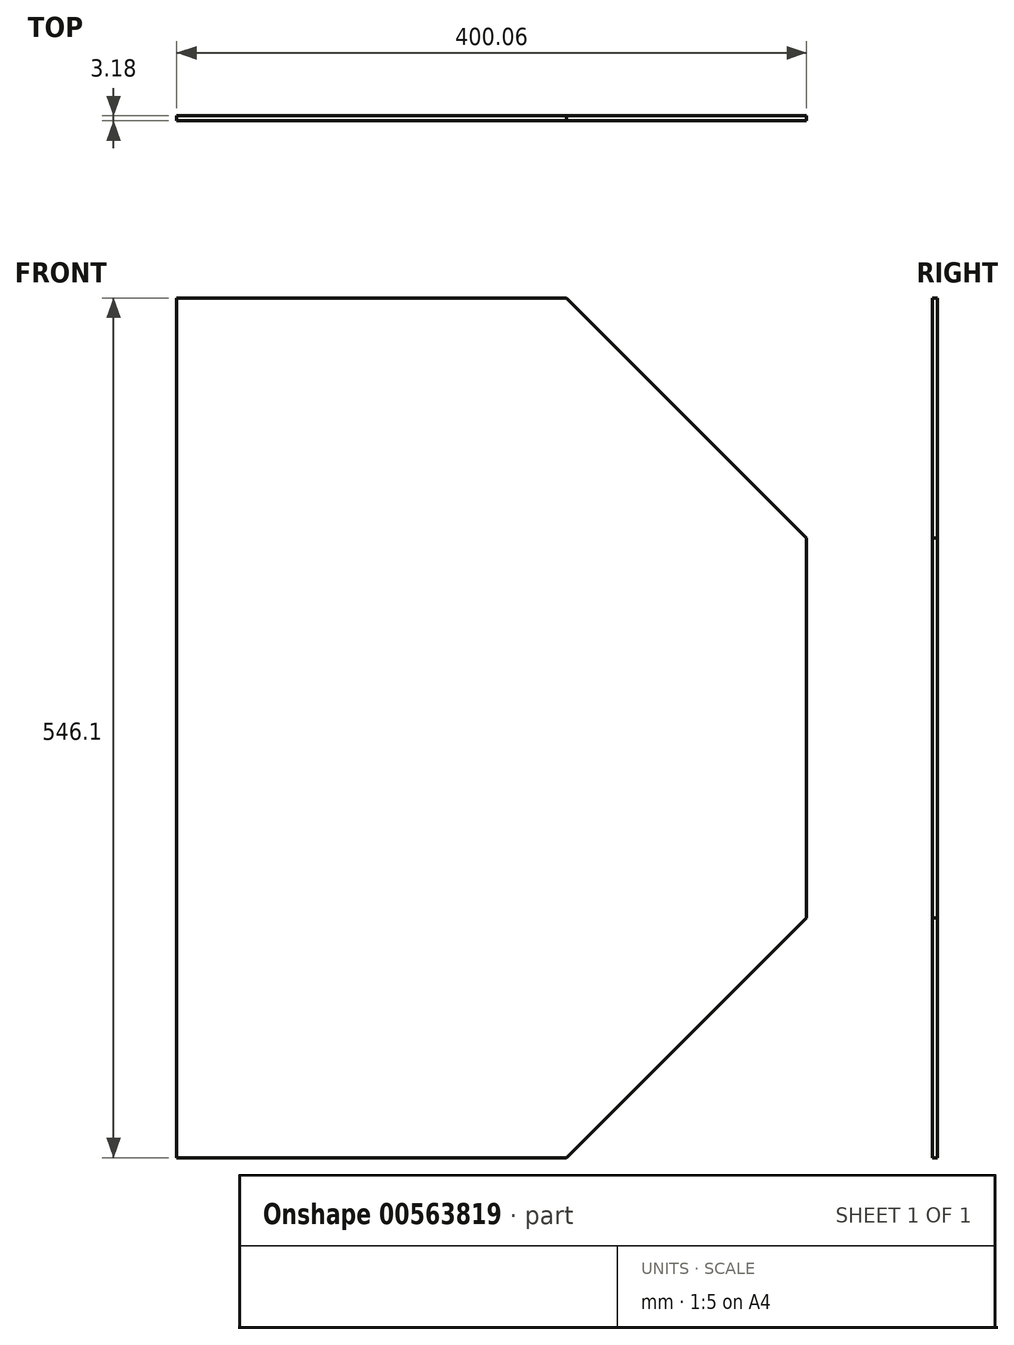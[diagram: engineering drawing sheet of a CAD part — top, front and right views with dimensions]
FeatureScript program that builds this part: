
annotation { "Feature Type Name" : "Feature", "Feature Type Description" : "" }
export const myFeature = defineFeature(function(context is Context, id is Id, definition is map)
    precondition{}
    {
        {
            var Q0;
            Q0=qCreatedBy(makeId("Front.planeOp"),FACE);
            var sketch = newSketch(context, id + "F0", { "sketchPlane" : qUnion([Q0])});
            skLineSegment(sketch, "E0.bottom", {"start": v(-200.03, 273.05) * mm, "end": v(200.03, 273.05) * mm});
            skLineSegment(sketch, "E0.top", {"start": v(-200.03, -273.05) * mm, "end": v(200.02, -273.05) * mm});
            skLineSegment(sketch, "E0.left", {"start": v(-200.02, 273.05) * mm, "end": v(-200.03, -273.05) * mm});
            skLineSegment(sketch, "E0.right", {"start": v(200.03, 273.05) * mm, "end": v(200.02, -273.05) * mm});
            skPoint(sketch, "E0.middle", {"position": v(0, 0) * mm});
            skLineSegment(sketch, "E1", {"start": v(-200.03, -273.05) * mm, "end": v(47.62, -273.05) * mm});
            skLineSegment(sketch, "E2", {"start": v(47.62, -273.05) * mm, "end": v(47.62, 273.05) * mm});
            skLineSegment(sketch, "E3", {"start": v(47.62, -273.05) * mm, "end": v(200.03, -120.65) * mm});
            skLineSegment(sketch, "E4", {"start": v(47.62, 273.05) * mm, "end": v(200.03, 120.65) * mm});
            skSolve(sketch);
        }
        {
            var Q0;
            {var subQ0=sQuery(id+"F0.wireOp",EDGE,"E0.left");Q0=makeQuery(id+"F0.imprint","IMPRINT",FACE,{"disambiguationData":[TD([[makeQuery(id+"F0.imprint","IMPRINT",EDGE,{"derivedFrom":subQ0}),1.0]])]});}
            var Q1;
            Q1=makeQuery(id+"F0.imprint","IMPRINT",FACE,{"disambiguationData":[TD([[makeQuery(id+"F0.imprint","IMPRINT",EDGE,{"derivedFrom":sQuery(id+"F0.wireOp",EDGE,"E2")}),-1.0]])]});
            extrude(context, id + "F1", {"entities" : qUnion([Q0, Q1]), "endBound" : BoundingType.SYMMETRIC, "depth" : 3.17 * mm, "offsetDistance" : 25.4 * mm});
        }
    });
